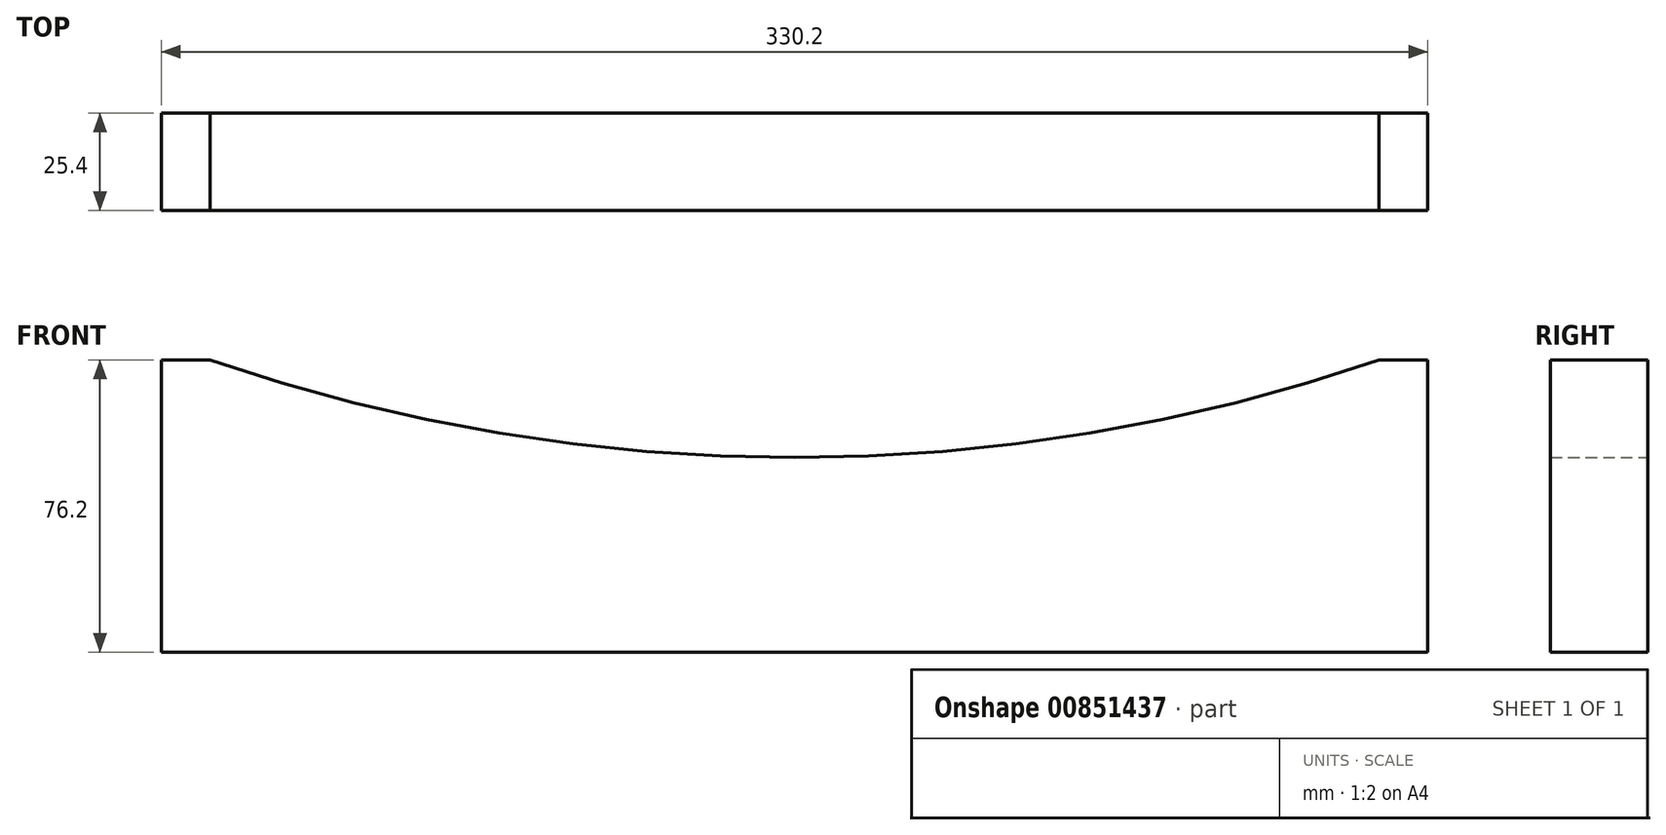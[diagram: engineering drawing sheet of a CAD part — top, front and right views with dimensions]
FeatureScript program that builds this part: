
annotation { "Feature Type Name" : "Feature", "Feature Type Description" : "" }
export const myFeature = defineFeature(function(context is Context, id is Id, definition is map)
    precondition{}
    {
        {
            var Q0;
            Q0=qCreatedBy(makeId("Front.planeOp"),FACE);
            var sketch = newSketch(context, id + "F0", { "sketchPlane" : qUnion([Q0])});
            skLineSegment(sketch, "E0", {"start": v(0, 0) * mm, "end": v(330.2, 0) * mm});
            skLineSegment(sketch, "E1", {"start": v(330.2, 0) * mm, "end": v(330.2, 76.2) * mm});
            skLineSegment(sketch, "E2", {"start": v(330.2, 76.2) * mm, "end": v(317.5, 76.2) * mm});
            skLineSegment(sketch, "E3", {"start": v(0, 0) * mm, "end": v(0, 76.2) * mm});
            skLineSegment(sketch, "E4", {"start": v(0, 76.2) * mm, "end": v(12.7, 76.2) * mm});
            skArc(sketch, "E5", {"start": v(12.7, 76.2) * mm, "mid": v(165.1, 50.8) * mm, "end": v(317.5, 76.2) * mm});
            skPoint(sketch, "E6", {"position": v(165.1, 50.8) * mm});
            skSolve(sketch);
        }
        {
            var Q0;
            Q0 = qSketchRegion(id + "F0", true);
            extrude(context, id + "F1", {"entities" : qUnion([Q0]), "depth" : 25.4 * mm, "offsetDistance" : 25.4 * mm});
        }
    });
